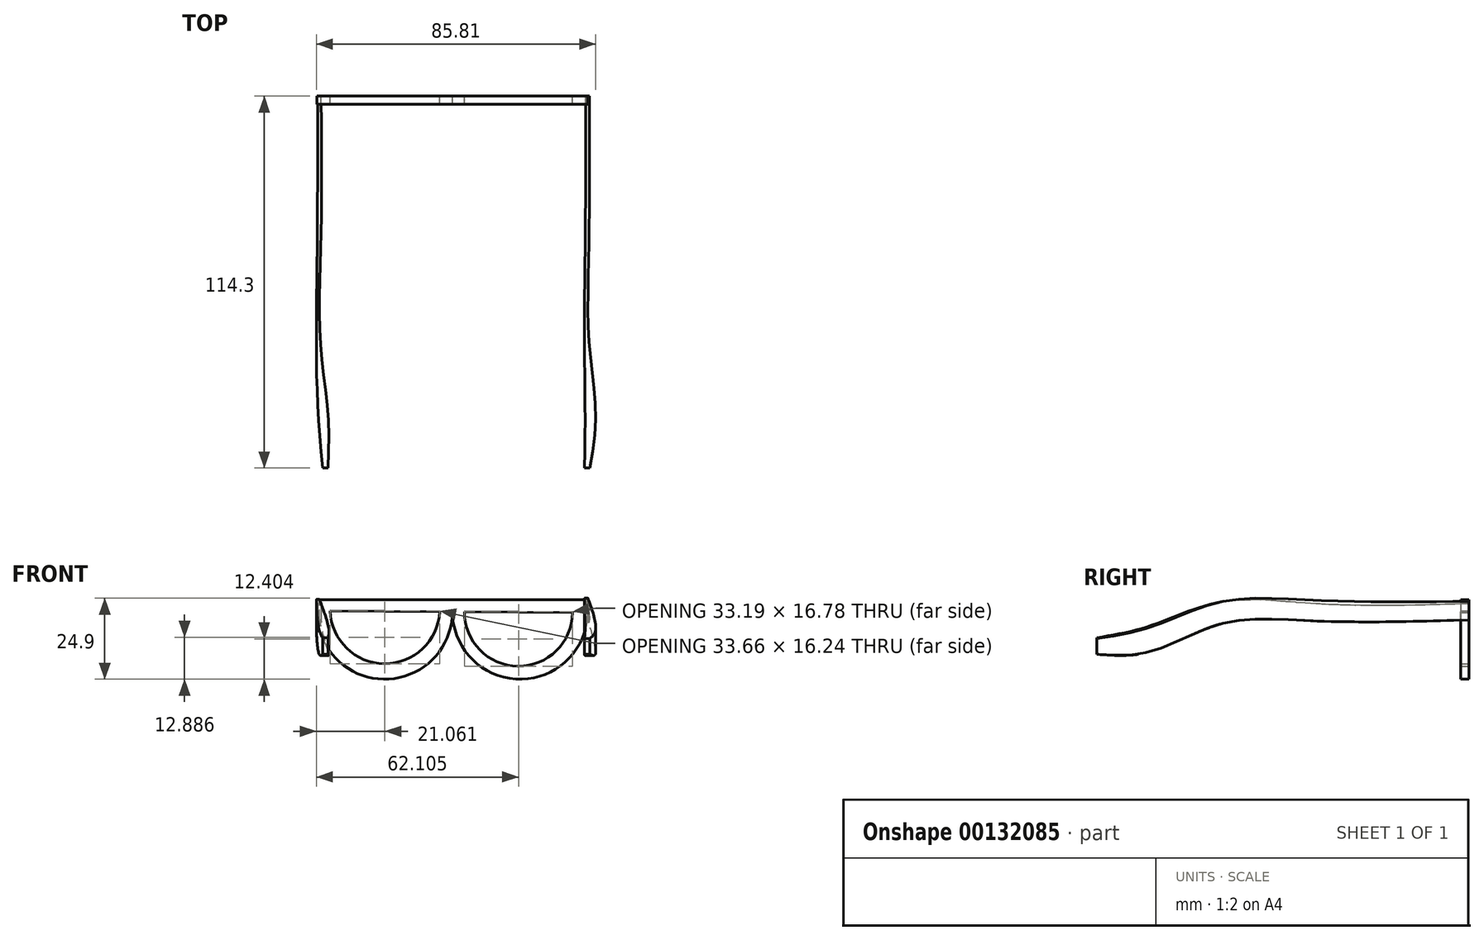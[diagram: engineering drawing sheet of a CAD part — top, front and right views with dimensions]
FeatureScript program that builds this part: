
annotation { "Feature Type Name" : "Feature", "Feature Type Description" : "" }
export const myFeature = defineFeature(function(context is Context, id is Id, definition is map)
    precondition{}
    {
        {
            var Q0;
            Q0=qCreatedBy(makeId("Front.planeOp"),FACE);
            cPlane(context, id + "F0", {"entities" : qUnion([Q0]), "cplaneType" : CPlaneType.OFFSET, "offset" : 101.6 * mm, "width" : 152.4 * mm, "height" : 152.4 * mm});
        }
        {
            var Q0;
            Q0=qCreatedBy(makeId("Front.planeOp"),FACE);
            cPlane(context, id + "F1", {"entities" : qUnion([Q0]), "cplaneType" : CPlaneType.OFFSET, "offset" : 76.2 * mm, "width" : 152.4 * mm, "height" : 152.4 * mm});
        }
        {
            var Q0;
            Q0=qCreatedBy(id+"F0.planeOp",FACE);
            var sketch = newSketch(context, id + "F2", { "sketchPlane" : qUnion([Q0])});
            skLineSegment(sketch, "E0.bottom", {"start": v(-42.33, 7.62) * mm, "end": v(-39.37, 7.62) * mm});
            skLineSegment(sketch, "E0.top", {"start": v(-42.33, 0) * mm, "end": v(-39.37, 0) * mm});
            skLineSegment(sketch, "E0.left", {"start": v(-42.33, 7.62) * mm, "end": v(-42.33, 0) * mm});
            skLineSegment(sketch, "E0.right", {"start": v(-39.37, 7.62) * mm, "end": v(-39.37, 0) * mm});
            skLineSegment(sketch, "E1.bottom", {"start": v(39.37, 0) * mm, "end": v(42.55, 0) * mm});
            skLineSegment(sketch, "E1.top", {"start": v(39.37, 7.2) * mm, "end": v(42.55, 7.2) * mm});
            skLineSegment(sketch, "E1.left", {"start": v(39.37, 0) * mm, "end": v(39.37, 7.2) * mm});
            skLineSegment(sketch, "E1.right", {"start": v(42.55, 0) * mm, "end": v(42.55, 7.2) * mm});
            skSolve(sketch);
        }
        {
            var Q0;
            Q0=qCreatedBy(id+"F1.planeOp",FACE);
            var sketch = newSketch(context, id + "F3", { "sketchPlane" : qUnion([Q0])});
            skLineSegment(sketch, "E2.bottom", {"start": v(-43.18, 16.09) * mm, "end": v(-41.91, 16.09) * mm});
            skLineSegment(sketch, "E2.top", {"start": v(-43.18, 9.31) * mm, "end": v(-41.91, 9.31) * mm});
            skLineSegment(sketch, "E2.left", {"start": v(-43.18, 16.09) * mm, "end": v(-43.18, 9.31) * mm});
            skLineSegment(sketch, "E2.right", {"start": v(-41.91, 16.09) * mm, "end": v(-41.91, 9.31) * mm});
            skLineSegment(sketch, "E3.bottom", {"start": v(39.16, 16.09) * mm, "end": v(40.64, 16.09) * mm});
            skLineSegment(sketch, "E3.top", {"start": v(39.16, 9.31) * mm, "end": v(40.64, 9.31) * mm});
            skLineSegment(sketch, "E3.left", {"start": v(39.16, 16.09) * mm, "end": v(39.16, 9.31) * mm});
            skLineSegment(sketch, "E3.right", {"start": v(40.64, 16.09) * mm, "end": v(40.64, 9.31) * mm});
            skSolve(sketch);
        }
        {
            var Q0;
            Q0=qCreatedBy(makeId("Front.planeOp"),FACE);
            var sketch = newSketch(context, id + "F4", { "sketchPlane" : qUnion([Q0])});
            skLineSegment(sketch, "E4.bottom", {"start": v(-42.76, 15.66) * mm, "end": v(-41.7, 15.66) * mm});
            skLineSegment(sketch, "E4.top", {"start": v(-42.76, 10.58) * mm, "end": v(-41.7, 10.58) * mm});
            skLineSegment(sketch, "E4.left", {"start": v(-42.76, 15.66) * mm, "end": v(-42.76, 10.58) * mm});
            skLineSegment(sketch, "E4.right", {"start": v(-41.7, 15.66) * mm, "end": v(-41.7, 10.58) * mm});
            skLineSegment(sketch, "E5.bottom", {"start": v(39.58, 16.3) * mm, "end": v(40.64, 16.3) * mm});
            skLineSegment(sketch, "E5.top", {"start": v(39.58, 10.58) * mm, "end": v(40.64, 10.58) * mm});
            skLineSegment(sketch, "E5.left", {"start": v(39.58, 16.3) * mm, "end": v(39.58, 10.58) * mm});
            skLineSegment(sketch, "E5.right", {"start": v(40.64, 16.3) * mm, "end": v(40.64, 10.58) * mm});
            skSolve(sketch);
        }
        {
            var Q0;
            Q0=qCreatedBy(makeId("Front.planeOp"),FACE);
            cPlane(context, id + "F5", {"entities" : qUnion([Q0]), "cplaneType" : CPlaneType.OFFSET, "offset" : 50.8 * mm, "width" : 152.4 * mm, "height" : 152.4 * mm});
        }
        {
            var Q0;
            Q0=qCreatedBy(id+"F5.planeOp",FACE);
            var sketch = newSketch(context, id + "F6", { "sketchPlane" : qUnion([Q0])});
            skLineSegment(sketch, "E6.bottom", {"start": v(-42.97, 15.88) * mm, "end": v(-41.91, 15.88) * mm});
            skLineSegment(sketch, "E6.top", {"start": v(-42.97, 10.37) * mm, "end": v(-41.91, 10.37) * mm});
            skLineSegment(sketch, "E6.left", {"start": v(-42.97, 15.88) * mm, "end": v(-42.97, 10.37) * mm});
            skLineSegment(sketch, "E6.right", {"start": v(-41.91, 15.88) * mm, "end": v(-41.91, 10.37) * mm});
            skLineSegment(sketch, "E7.bottom", {"start": v(39.37, 16.72) * mm, "end": v(40.43, 16.72) * mm});
            skLineSegment(sketch, "E7.top", {"start": v(39.37, 10.37) * mm, "end": v(40.43, 10.37) * mm});
            skLineSegment(sketch, "E7.left", {"start": v(39.37, 16.72) * mm, "end": v(39.37, 10.37) * mm});
            skLineSegment(sketch, "E7.right", {"start": v(40.43, 16.72) * mm, "end": v(40.43, 10.37) * mm});
            skSolve(sketch);
        }
        {
            var Q0;
            Q0=qCreatedBy(makeId("Front.planeOp"),FACE);
            cPlane(context, id + "F7", {"entities" : qUnion([Q0]), "cplaneType" : CPlaneType.OFFSET, "offset" : 114.3 * mm, "width" : 152.4 * mm, "height" : 152.4 * mm});
        }
        {
            var Q0;
            Q0=qCreatedBy(id+"F7.planeOp",FACE);
            var sketch = newSketch(context, id + "F8", { "sketchPlane" : qUnion([Q0])});
            skLineSegment(sketch, "E8.bottom", {"start": v(-41.28, 5.08) * mm, "end": v(-39.58, 5.08) * mm});
            skLineSegment(sketch, "E8.top", {"start": v(-41.28, 0) * mm, "end": v(-39.58, 0) * mm});
            skLineSegment(sketch, "E8.left", {"start": v(-41.28, 5.08) * mm, "end": v(-41.28, 0) * mm});
            skLineSegment(sketch, "E8.right", {"start": v(-39.58, 5.08) * mm, "end": v(-39.58, 0) * mm});
            skLineSegment(sketch, "E9.bottom", {"start": v(39.16, 4.87) * mm, "end": v(40.85, 4.87) * mm});
            skLineSegment(sketch, "E9.top", {"start": v(39.16, 0) * mm, "end": v(40.85, 0) * mm});
            skLineSegment(sketch, "E9.left", {"start": v(39.16, 4.87) * mm, "end": v(39.16, 0) * mm});
            skLineSegment(sketch, "E9.right", {"start": v(40.85, 4.87) * mm, "end": v(40.85, 0) * mm});
            skSolve(sketch);
        }
        {
            var Q0;
            Q0=makeQuery(id+"F8.imprint","IMPRINT",FACE,{"disambiguationData":[TD([[makeQuery(id+"F8.imprint","IMPRINT",EDGE,{"derivedFrom":sQuery(id+"F8.wireOp",EDGE,"E8.bottom")}),-1.0]])]});
            var Q1;
            Q1=makeQuery(id+"F2.imprint","IMPRINT",FACE,{"disambiguationData":[TD([[makeQuery(id+"F2.imprint","IMPRINT",EDGE,{"derivedFrom":sQuery(id+"F2.wireOp",EDGE,"E0.bottom")}),-1.0]])]});
            var Q2;
            Q2=makeQuery(id+"F3.imprint","IMPRINT",FACE,{"disambiguationData":[TD([[makeQuery(id+"F3.imprint","IMPRINT",EDGE,{"derivedFrom":sQuery(id+"F3.wireOp",EDGE,"E2.bottom")}),-1.0]])]});
            var Q3;
            Q3=makeQuery(id+"F6.imprint","IMPRINT",FACE,{"disambiguationData":[TD([[makeQuery(id+"F6.imprint","IMPRINT",EDGE,{"derivedFrom":sQuery(id+"F6.wireOp",EDGE,"E6.bottom")}),-1.0]])]});
            var Q4;
            Q4=makeQuery(id+"F4.imprint","IMPRINT",FACE,{"disambiguationData":[TD([[makeQuery(id+"F4.imprint","IMPRINT",EDGE,{"derivedFrom":sQuery(id+"F4.wireOp",EDGE,"E4.bottom")}),-1.0]])]});
            loft(context, id + "F9", {"sheetProfilesArray" : [{ "sheetProfileEntities" : qUnion([Q0]) }, { "sheetProfileEntities" : qUnion([Q1]) }, { "sheetProfileEntities" : qUnion([Q2]) }, { "sheetProfileEntities" : qUnion([Q3]) }, { "sheetProfileEntities" : qUnion([Q4]) }]});
        }
        {
            var Q0;
            Q0=makeQuery(id+"F8.imprint","IMPRINT",FACE,{"disambiguationData":[TD([[makeQuery(id+"F8.imprint","IMPRINT",EDGE,{"derivedFrom":sQuery(id+"F8.wireOp",EDGE,"E9.bottom")}),-1.0]])]});
            var Q1;
            Q1=makeQuery(id+"F2.imprint","IMPRINT",FACE,{"disambiguationData":[TD([[makeQuery(id+"F2.imprint","IMPRINT",EDGE,{"derivedFrom":sQuery(id+"F2.wireOp",EDGE,"E1.bottom")}),1.0]])]});
            var Q2;
            Q2=makeQuery(id+"F3.imprint","IMPRINT",FACE,{"disambiguationData":[TD([[makeQuery(id+"F3.imprint","IMPRINT",EDGE,{"derivedFrom":sQuery(id+"F3.wireOp",EDGE,"E3.bottom")}),-1.0]])]});
            var Q3;
            Q3=makeQuery(id+"F6.imprint","IMPRINT",FACE,{"disambiguationData":[TD([[makeQuery(id+"F6.imprint","IMPRINT",EDGE,{"derivedFrom":sQuery(id+"F6.wireOp",EDGE,"E7.bottom")}),-1.0]])]});
            var Q4;
            Q4=makeQuery(id+"F4.imprint","IMPRINT",FACE,{"disambiguationData":[TD([[makeQuery(id+"F4.imprint","IMPRINT",EDGE,{"derivedFrom":sQuery(id+"F4.wireOp",EDGE,"E5.bottom")}),-1.0]])]});
            loft(context, id + "F10", {"sheetProfilesArray" : [{ "sheetProfileEntities" : qUnion([Q0]) }, { "sheetProfileEntities" : qUnion([Q1]) }, { "sheetProfileEntities" : qUnion([Q2]) }, { "sheetProfileEntities" : qUnion([Q3]) }, { "sheetProfileEntities" : qUnion([Q4]) }]});
        }
        {
            var Q0;
            Q0=qCreatedBy(makeId("Front.planeOp"),FACE);
            var sketch = newSketch(context, id + "F11", { "sketchPlane" : qUnion([Q0])});
            skLineSegment(sketch, "E10.bottom", {"start": v(40.22, 16.72) * mm, "end": v(-42.97, 16.72) * mm});
            skLineSegment(sketch, "E10.top", {"start": v(40.22, 13.12) * mm, "end": v(-42.97, 13.12) * mm});
            skLineSegment(sketch, "E10.left", {"start": v(40.22, 16.72) * mm, "end": v(40.22, 13.12) * mm});
            skLineSegment(sketch, "E10.right", {"start": v(-42.97, 16.72) * mm, "end": v(-42.97, 13.12) * mm});
            skArc(sketch, "E11", {"start": v(-1.38, 13.12) * mm, "mid": v(19.42, -7.67) * mm, "end": v(40.22, 13.12) * mm});
            skArc(sketch, "E12", {"start": v(-42.97, 13.12) * mm, "mid": v(-22.17, -7.67) * mm, "end": v(-1.38, 13.12) * mm});
            skSolve(sketch);
        }
        {
            var Q0;
            Q0 = qSketchRegion(id + "F11", true);
            extrude(context, id + "F12", {"entities" : qUnion([Q0]), "depth" : 2.54 * mm});
        }
        {
            var Q0;
            Q0=makeQuery(id+"F12.opExtrude","CAP_FACE",FACE,{"disambiguationData":[OSD([sQuery(id+"F11.wireOp",EDGE,"E10.bottom"),sQuery(id+"F11.wireOp",EDGE,"E10.left"),sQuery(id+"F11.wireOp",EDGE,"E10.right"),sQuery(id+"F11.wireOp",EDGE,"E11"),sQuery(id+"F11.wireOp",EDGE,"E12")])],"isStart":true});
            var sketch = newSketch(context, id + "F13", { "sketchPlane" : qUnion([Q0])});
            skArc(sketch, "E13", {"start": v(-35.52, 12.76) * mm, "mid": v(-18.74, -3.65) * mm, "end": v(-2.33, 13.12) * mm});
            skArc(sketch, "E14", {"start": v(5.3, 13.12) * mm, "mid": v(22.22, -2.9) * mm, "end": v(38.95, 13.34) * mm});
            skLineSegment(sketch, "E15", {"start": v(-35.52, 12.76) * mm, "end": v(-2.33, 13.12) * mm});
            skLineSegment(sketch, "E16", {"start": v(5.3, 13.12) * mm, "end": v(38.95, 13.34) * mm});
            skSolve(sketch);
        }
        {
            var Q0;
            Q0=makeQuery(id+"F13.imprint","IMPRINT",FACE,{"disambiguationData":[TD([[makeQuery(id+"F13.imprint","IMPRINT",EDGE,{"derivedFrom":sQuery(id+"F13.wireOp",EDGE,"E13")}),1.0]])]});
            extrude(context, id + "F14", {"entities" : qUnion([Q0]), "operationType" : NewBodyOperationType.REMOVE, "oppositeDirection" : true, "depth" : 25.4 * mm});
        }
        {
            var Q0;
            Q0 = qSketchRegion(id + "F13", true);
            extrude(context, id + "F15", {"entities" : qUnion([Q0]), "operationType" : NewBodyOperationType.REMOVE, "oppositeDirection" : true, "depth" : 25.4 * mm});
        }
    });
